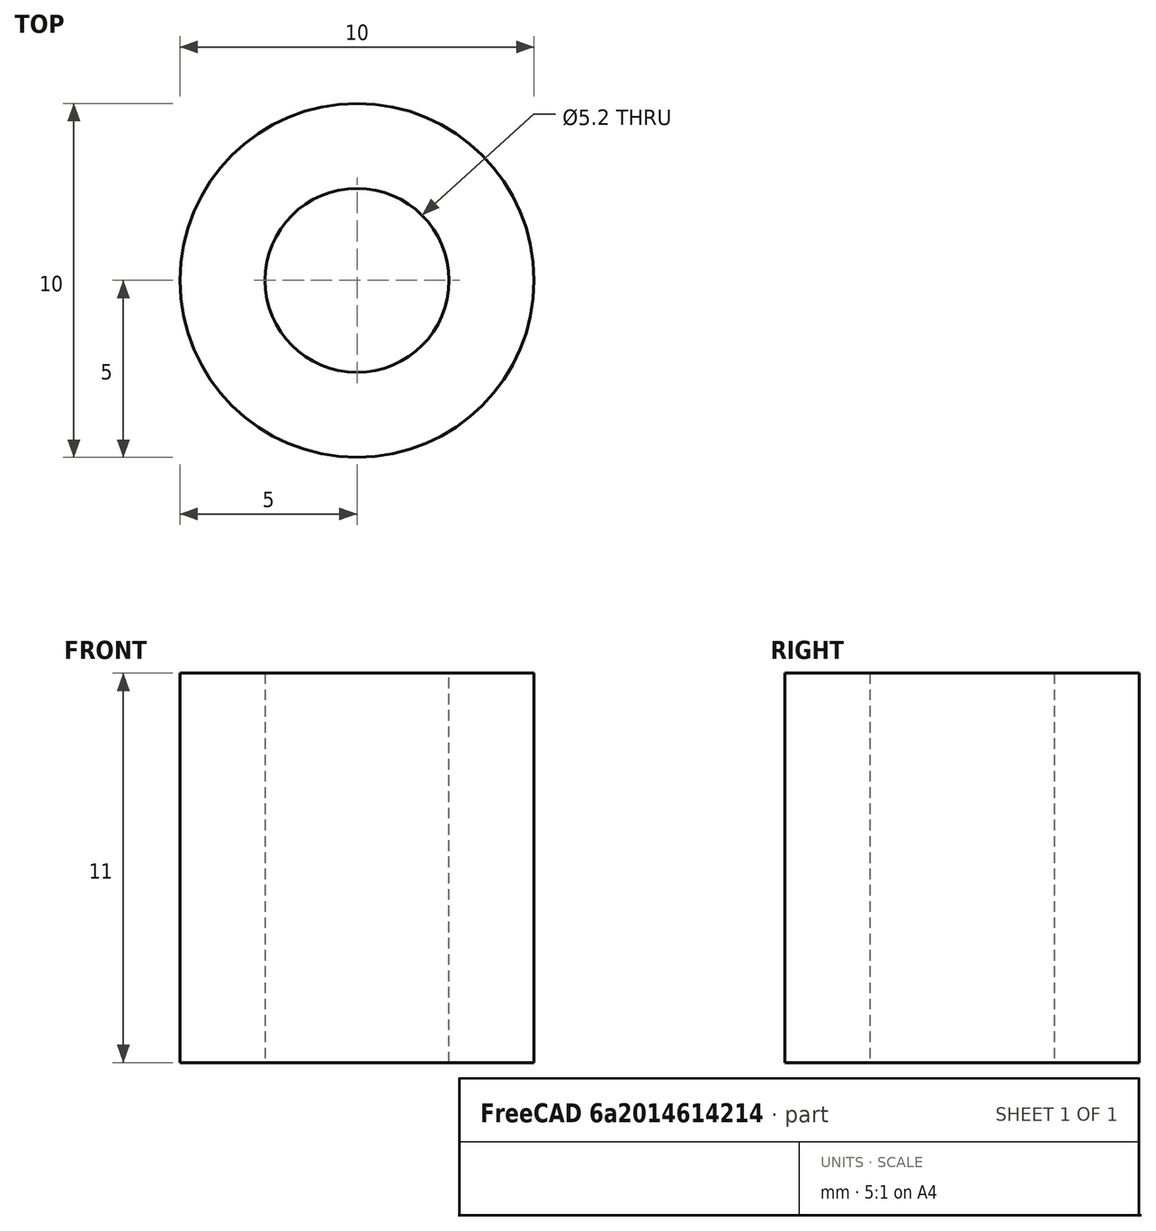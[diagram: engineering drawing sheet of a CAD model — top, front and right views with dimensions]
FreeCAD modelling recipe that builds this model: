
FCSTD DOCUMENT  (FreeCAD 1.0R38806 (Git))
Label: idler_spacer_11
License: All rights reserved
LicenseURL: http://en.wikipedia.org/wiki/All_rights_reserved
objects: Sketcher::SketchObject×1, PartDesign::Pad×1, PartDesign::Body×1
note: 6 computed .brp shape members not serialized (recipe doc carries the construction recipe); baked Part::Feature solids carry a one-line shape summary decoded from their .brp

FEATURE [Sketcher::SketchObject] Sketch
  ArcFitTolerance = 1e-06
  AttachmentSupport = -> [XY_Plane]
  FullyConstrained = true
  MakeInternals = false
  MapMode = 5
  sketch-geometry (2):
    g0: Circle CenterX=0 CenterY=0 CenterZ=0 NormalX=0 NormalY=0 NormalZ=1 AngleXU=0 Radius=5
    g1: Circle CenterX=0 CenterY=0 CenterZ=0 NormalX=0 NormalY=0 NormalZ=1 AngleXU=0 Radius=2.6
  constraints (5):
    c: Coincident(g0,g-1)
    c: PointOnObject(g1,g-1)
    c: Diameter(g0) = 10
    c: Diameter(g1) = 5.2
    c: DistanceX(g0,g1) = 0
FEATURE [PartDesign::Pad] Pad
  Direction = (0,0,1)
  Length = 11
  Length2 = 10
  Profile = -> Sketch
  ReferenceAxis = -> Sketch [N_Axis]
  Suppressed = false
  Type = 0
FEATURE [PartDesign::Body] Body
  AllowCompound = false
  Group = -> [Sketch,Pad]
  Origin = -> Origin
  Tip = -> Pad
